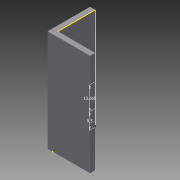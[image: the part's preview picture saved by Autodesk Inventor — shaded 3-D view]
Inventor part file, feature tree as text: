
AUTODESK INVENTOR PART (.ipt)
format: ipt  version: 2014 SP1 (Build 180222100, 222)  size: 78,336 bytes
history: native  units: mm
features: sketch x2, extrude x1
ambient origin geometry x8: Origin, YZ Plane, XZ Plane, XY Plane, X Axis, Y Axis, Z Axis, Center Point
bodies: Solid1 (feature_tree)
feature tree (3):
  extrude  "Extrusion1"  Depth=3.0mm
  sketch  "Sketch2"  dims[d2=22.0mm d3=22.0mm d4=60.0mm d5=0.0mm d6=9.5mm d7=13.665mm]
  sketch  "Sketch1"  dims[d0=25.0mm d1=3.0mm]
